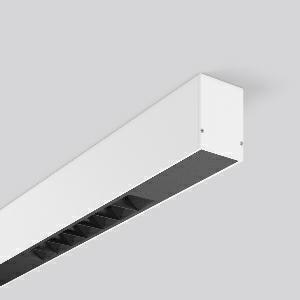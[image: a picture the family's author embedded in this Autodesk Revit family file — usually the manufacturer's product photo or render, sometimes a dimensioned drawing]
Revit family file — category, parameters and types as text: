
# Revit family: less_is_more_beamline_312484_002_76_9a45
name_source: partatom
category: Lighting Fixtures
units: mm (PartAtom-declared; Revit-internal decimal feet)

## family parameters
Cut with Voids When Loaded = No
Host = Face
Light Source = No
Part Type = Normal
Room Calculation Point = No
Round Connector Dimension = Use Diameter
Shared = No

## types (1)
- LESS IS MORE BEAMLINE (1 x LED Modul 930, 975 lm, 3000)
    Apparent Load = 23 VA
    CIE Flux Codes = 100 100 100 100 100
    Color Rendering = 90
    Color Temperature = 3000
    Default Elevation = 1800 mm
    Description = Series: LESS IS MORE BEAMLINE
Linear ceiling and wall luminaire for aesthetically sophisticated lighting. Luminaire with two LED light units. Housing: extruded aluminium profile, powder-coated. End cap aluminium powder-coated. LED light unit with MRS technology: Mini-Reflector-System made of metallised thermoplastic with prismatic black glare-suppressing frame for pleasant glare-free light (RUG < 10). Each LED light unit has 7 reflector elements. Medium beam light distribution. LED unit with integrated converter interchangeable and removable. Suitable for through-wiring. 
Colour: traffic white, matt (RAL 9016)
Length: 1127 mm
Width: 57 mm
Height: 75 mm
Lamp: LED
Socket: without socket
Colour temperature: 3000K
Colour rendering index (CRI): 90
System power: 23 W
Rated luminous flux: 1950 lm
Luminous efficiency: 85 lm/W
Control gear: Converter, dimmable, DALI
Protection class: I
Type of protection: IP 20
    Height = 75 mm
    Lamp = 1 x LED Modul 930
    Lamp Light Flux = 975 lm
    Lamp count = 1
    Length = 1127 mm
    Lifetime = 50000 h
    Luminous efficacy = 85 lm/W
    Manufacturer = RZB
    ModVariant = No
    Model = 312484.002.76
    Mounting Place = Ceiling, Wall
    Mounting Type = Surface mounted
    Number of Poles = 1
    OnlyDefault = Yes
    Power Factor = 1
    Product Name = LESS IS MORE BEAMLINE
    Product group = Surface mounted LED linear luminaires
    ProductGroupID = 307
    Protection Class = Protection class I
    Protection Degree = IP 20
    RLX_Detail_Level = 1
    RLX_Emergency_Light_Flux = 0 lm
    RLX_Emergency_Type = 0
    RLX_Emergency_Type_DB = No
    RlxData = <blob elided: 26917 chars, md5=96d72a64>
    Socket = socket
    Standby Power = 0 W
    System Light Flux = 1950 lm
    System Power = 23 W
    Type Comments = Product without accessories
    Type Image = 312483.002.jpg
    URL = http://relux.com
    VarID = ---
    Voltage = 230 V
    Voltage Range = 220-240 V
    Weight = 0.00 kg
    Width = 57 mm

## geometry (parser evidence)
native form markers: Blend x4, Sweep x16
no freeform markers — native parametric forms only
